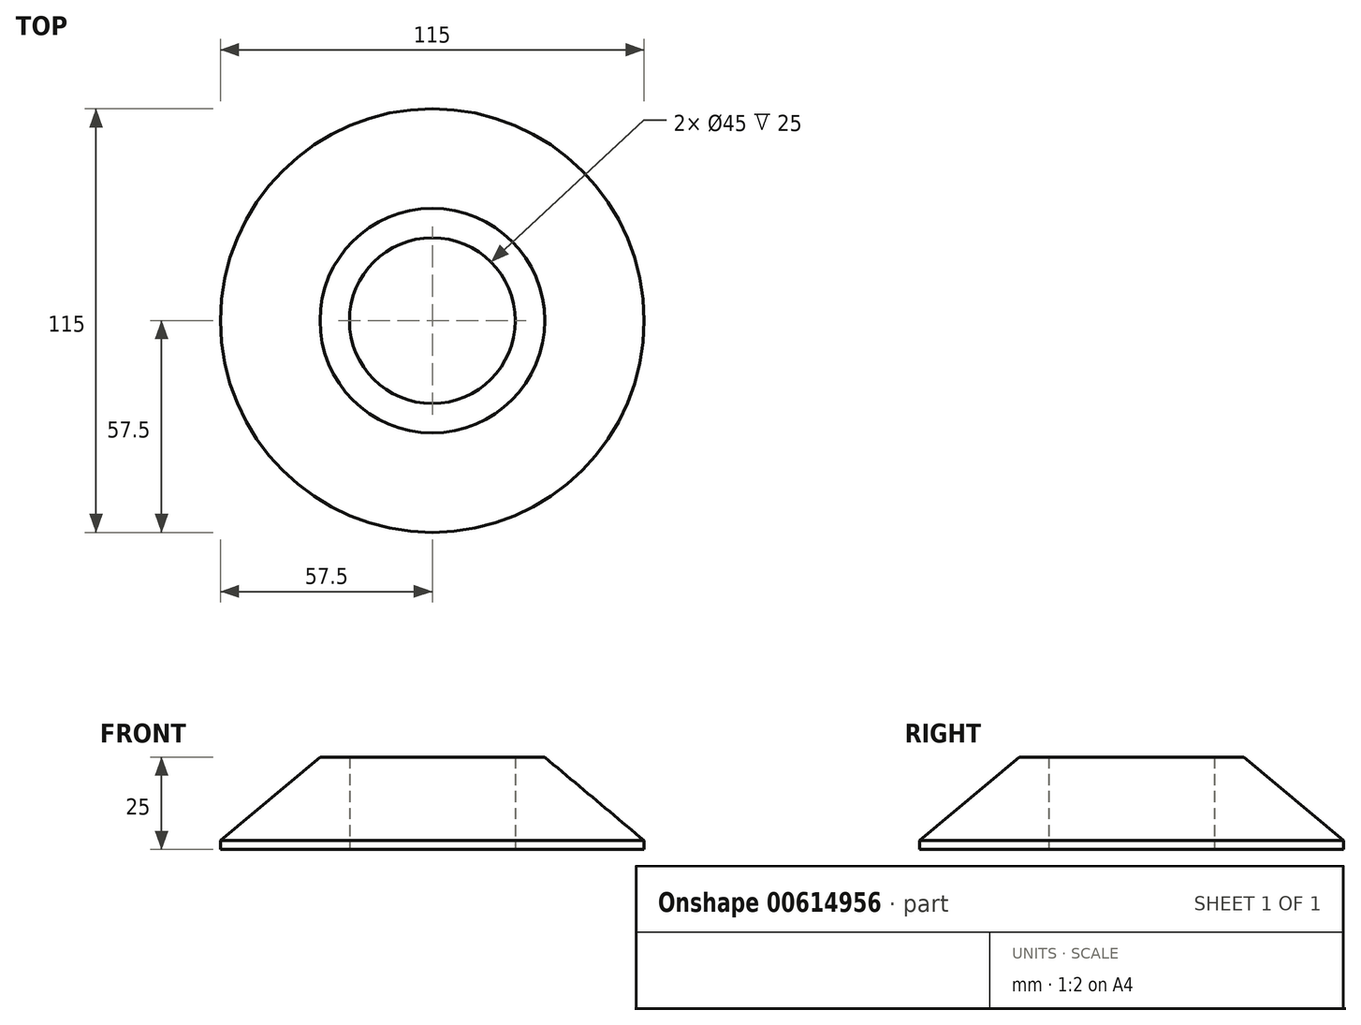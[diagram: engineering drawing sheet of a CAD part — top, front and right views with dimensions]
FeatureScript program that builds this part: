
annotation { "Feature Type Name" : "Feature", "Feature Type Description" : "" }
export const myFeature = defineFeature(function(context is Context, id is Id, definition is map)
    precondition{}
    {
        {
            var Q0;
            Q0=qCreatedBy(makeId("Top.planeOp"),FACE);
            var sketch = newSketch(context, id + "F0", { "sketchPlane" : qUnion([Q0])});
            skCircle(sketch, "E0", {"center": v(0, 0) * mm, "radius": 22.5 * mm});
            skCircle(sketch, "E1", {"center": v(0, 0) * mm, "radius": 57.5 * mm});
            skSolve(sketch);
        }
        {
            var Q0;
            Q0=makeQuery(id+"F0.imprint","IMPRINT",FACE,{"disambiguationData":[TD([[makeQuery(id+"F0.imprint","IMPRINT",EDGE,{"derivedFrom":sQuery(id+"F0.wireOp",EDGE,"E0")}),-1.0]])]});
            var Q1;
            Q1 = qSketchRegion(id + "F0", true);
            extrude(context, id + "F1", {"entities" : qUnion([Q0, Q1]), "depth" : 25 * mm, "offsetDistance" : 25 * mm});
        }
        {
            var Q0;
            Q0=makeQuery(id+"F1.opExtrude","CAP_EDGE",EDGE,{"disambiguationData":[OSD([sQuery(id+"F0.wireOp",EDGE,"E1")])],"isStart":false});
            chamfer(context, id + "F2", {"entities" : qUnion([Q0]), "chamferType" : ChamferType.OFFSET_ANGLE, "width" : 27 * mm, "oppositeDirection" : false, "angle" : 40 * degree, "tangentPropagation" : true});
        }
    });
